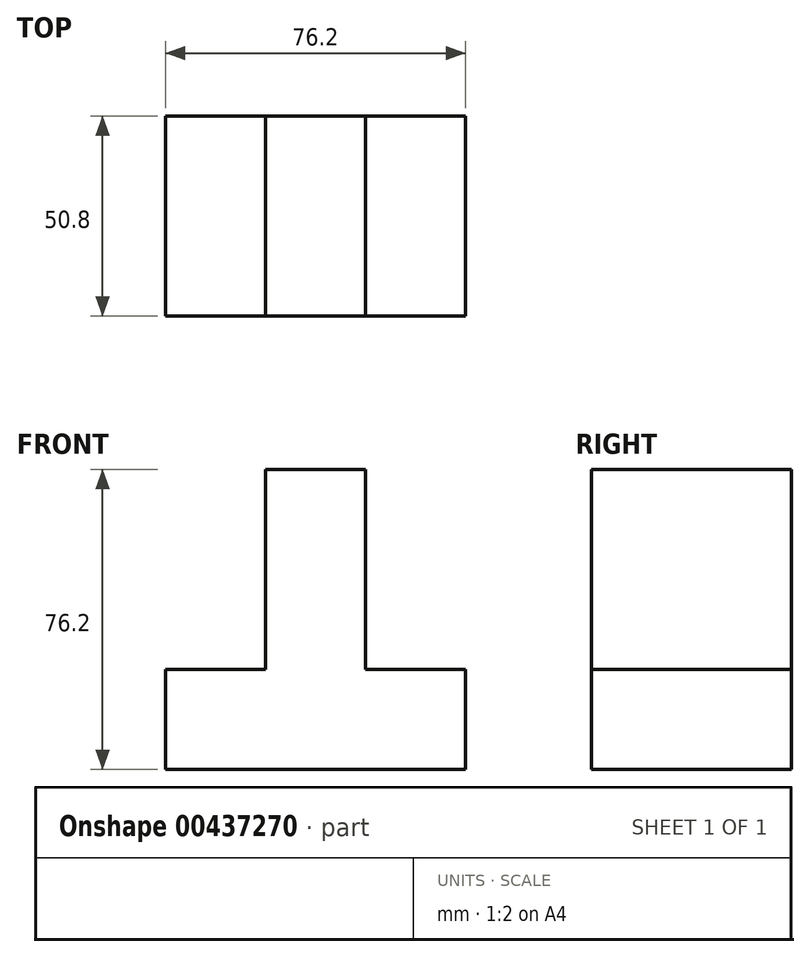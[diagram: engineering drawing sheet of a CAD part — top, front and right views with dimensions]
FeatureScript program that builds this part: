
annotation { "Feature Type Name" : "Feature", "Feature Type Description" : "" }
export const myFeature = defineFeature(function(context is Context, id is Id, definition is map)
    precondition{}
    {
        {
            var Q0;
            Q0=qCreatedBy(makeId("Front.planeOp"),FACE);
            var sketch = newSketch(context, id + "F0", { "sketchPlane" : qUnion([Q0])});
            skLineSegment(sketch, "E0", {"start": v(50.8, 0) * mm, "end": v(-25.4, 0) * mm});
            skLineSegment(sketch, "E1", {"start": v(-25.4, 0) * mm, "end": v(-25.4, 25.4) * mm});
            skLineSegment(sketch, "E2", {"start": v(-25.4, 25.4) * mm, "end": v(0, 25.4) * mm});
            skLineSegment(sketch, "E3", {"start": v(0, 25.4) * mm, "end": v(0, 76.2) * mm});
            skLineSegment(sketch, "E4", {"start": v(0, 76.2) * mm, "end": v(25.4, 76.2) * mm});
            skLineSegment(sketch, "E5", {"start": v(25.4, 76.2) * mm, "end": v(25.4, 25.4) * mm});
            skLineSegment(sketch, "E6", {"start": v(25.4, 25.4) * mm, "end": v(50.8, 25.4) * mm});
            skLineSegment(sketch, "E7", {"start": v(50.8, 25.4) * mm, "end": v(50.8, 0) * mm});
            skSolve(sketch);
        }
        {
            var Q0;
            Q0 = qSketchRegion(id + "F0", true);
            extrude(context, id + "F1", {"entities" : qUnion([Q0]), "depth" : 50.8 * mm});
        }
    });
